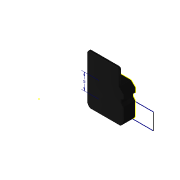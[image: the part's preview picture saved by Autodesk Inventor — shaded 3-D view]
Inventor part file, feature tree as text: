
AUTODESK INVENTOR PART (.ipt)
format: ipt  version: 2022 (Build 260153000, 153)  size: 278,016 bytes
history: native  units: mm
features: projected_geometry x14, extrude x3, sketch x3, fillet x1
ambient origin geometry x8: Origin, YZ Plane, XZ Plane, XY Plane, X Axis, Y Axis, Z Axis, Center Point
bodies: Volumenkörper1 (feature_tree)
feature tree (21):
  extrude  "Extrusion1"  TaperAngle=0.0deg  [1 undecoded]
  extrude  "Extrusion2"  Depth=5.0mm
  extrude  "Extrusion3"  [1 undecoded]
  sketch  "Skizze1"  dims[d0=10.0mm d1=0.0mm d2=0.0mm]
  sketch  "Skizze2"  dims[d3=3.0mm d4=0.5mm d5=0.0mm d6=0.0mm d8=5.0mm]
  projected_geometry  "Projizierte Kontur1"
  projected_geometry  "Projizierte Kontur2"
  projected_geometry  "Projizierte Kontur3"
  projected_geometry  "Projizierte Kontur4"
  projected_geometry  "Projizierte Kontur5"
  projected_geometry  "Projizierte Kontur6"
  projected_geometry  "Projizierte Kontur7"
  projected_geometry  "Projizierte Kontur8"
  projected_geometry  "Projizierte Kontur9"
  projected_geometry  "Projizierte Kontur10"
  projected_geometry  "Projizierte Kontur11"
  projected_geometry  "Projizierte Kontur12"
  projected_geometry  "Projizierte Kontur13"
  sketch  "Skizze3"  dims[d9=10.0mm d10=0.0mm]
  projected_geometry  "Projizierte Kontur14"
  fillet  "Fillet2"  [1 undecoded]
note: 3 required parameter values undecoded (feature->parameter linkage not recoverable at this tier; creation-order binding heuristic only, values carry confidence <= 0.55)
